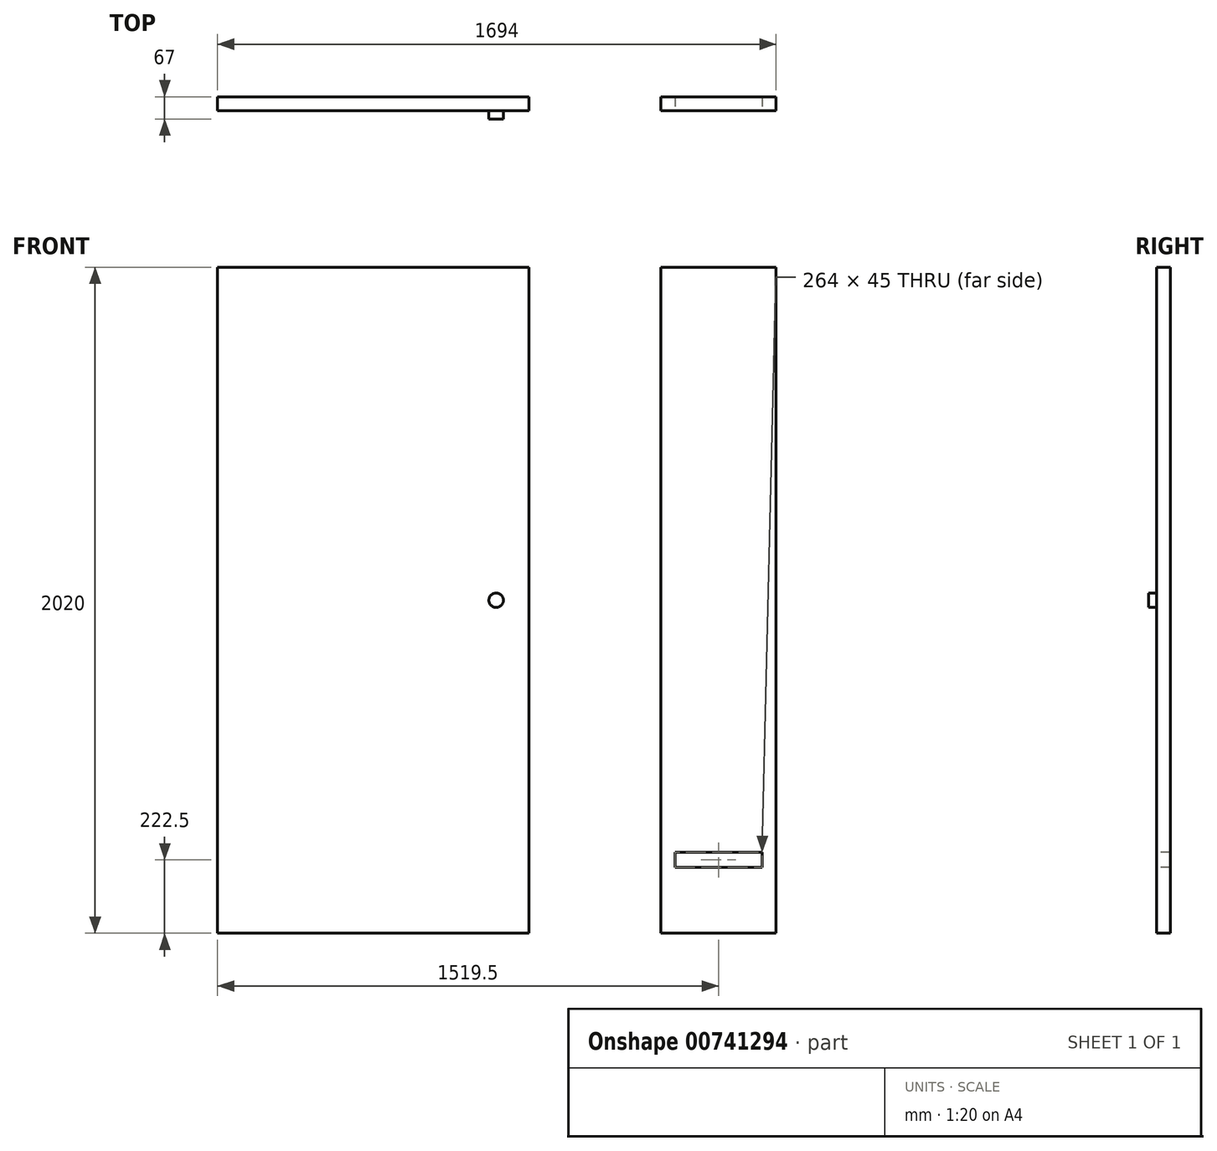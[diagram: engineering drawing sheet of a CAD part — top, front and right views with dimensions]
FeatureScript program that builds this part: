
annotation { "Feature Type Name" : "Feature", "Feature Type Description" : "" }
export const myFeature = defineFeature(function(context is Context, id is Id, definition is map)
    precondition{}
    {
        {
            var Q0;
            Q0=qCreatedBy(makeId("Front.planeOp"),FACE);
            var sketch = newSketch(context, id + "F0", { "sketchPlane" : qUnion([Q0])});
            skLineSegment(sketch, "E0.bottom", {"start": v(472.5, -1010) * mm, "end": v(-472.5, -1010) * mm});
            skLineSegment(sketch, "E0.top", {"start": v(472.5, 1010) * mm, "end": v(-472.5, 1010) * mm});
            skLineSegment(sketch, "E0.left", {"start": v(472.5, -1010) * mm, "end": v(472.5, 1010) * mm});
            skLineSegment(sketch, "E0.right", {"start": v(-472.5, -1010) * mm, "end": v(-472.5, 1010) * mm});
            skPoint(sketch, "E0.middle", {"position": v(0, 0) * mm});
            skSolve(sketch);
        }
        {
            var Q0;
            Q0 = qSketchRegion(id + "F0", true);
            extrude(context, id + "F1", {"entities" : qUnion([Q0]), "depth" : 42 * mm, "offsetDistance" : 25 * mm});
        }
        {
            var Q0;
            Q0=qCreatedBy(makeId("Front.planeOp"),FACE);
            var sketch = newSketch(context, id + "F2", { "sketchPlane" : qUnion([Q0])});
            skLineSegment(sketch, "E1.bottom", {"start": v(1221.5, -1010) * mm, "end": v(872.5, -1010) * mm});
            skLineSegment(sketch, "E1.top", {"start": v(1221.5, 1010) * mm, "end": v(872.5, 1010) * mm});
            skLineSegment(sketch, "E1.left", {"start": v(1221.5, -1010) * mm, "end": v(1221.5, 1010) * mm});
            skLineSegment(sketch, "E1.right", {"start": v(872.5, -1010) * mm, "end": v(872.5, 1010) * mm});
            skPoint(sketch, "E1.middle", {"position": v(1047, 0) * mm});
            skSolve(sketch);
        }
        {
            var Q0;
            Q0 = qSketchRegion(id + "F2", true);
            extrude(context, id + "F3", {"entities" : qUnion([Q0]), "depth" : 42 * mm, "offsetDistance" : 25 * mm});
        }
        {
            var Q0;
            Q0=makeQuery(id+"F3.opExtrude","CAP_FACE",FACE,{"disambiguationData":[OSD([sQuery(id+"F2.wireOp",EDGE,"E1.bottom"),sQuery(id+"F2.wireOp",EDGE,"E1.top"),sQuery(id+"F2.wireOp",EDGE,"E1.left"),sQuery(id+"F2.wireOp",EDGE,"E1.right")])],"isStart":false});
            var sketch = newSketch(context, id + "F4", { "sketchPlane" : qUnion([Q0])});
            skLineSegment(sketch, "E2.bottom", {"start": v(1179, -810) * mm, "end": v(915, -810) * mm});
            skLineSegment(sketch, "E2.top", {"start": v(1179, -765) * mm, "end": v(915, -765) * mm});
            skLineSegment(sketch, "E2.left", {"start": v(1179, -810) * mm, "end": v(1179, -765) * mm});
            skLineSegment(sketch, "E2.right", {"start": v(915, -810) * mm, "end": v(915, -765) * mm});
            skPoint(sketch, "E2.middle", {"position": v(1047, -787.5) * mm});
            skPoint(sketch, "E2.middle.positionSnap0", {"position": v(1047, 1010) * mm});
            skPoint(sketch, "E2.centerSnap0", {"position": v(1047, 1010) * mm});
            skSolve(sketch);
        }
        {
            var Q0;
            Q0=makeQuery(id+"F4.imprint","IMPRINT",FACE,{"disambiguationData":[TD([[makeQuery(id+"F4.imprint","IMPRINT",EDGE,{"derivedFrom":sQuery(id+"F4.wireOp",EDGE,"E2.bottom")}),-1.0]])]});
            extrude(context, id + "F5", {"entities" : qUnion([Q0]), "operationType" : NewBodyOperationType.REMOVE, "endBound" : BoundingType.THROUGH_ALL, "oppositeDirection" : true, "depth" : 25 * mm, "offsetDistance" : 25 * mm});
        }
        {
            var Q0;
            Q0=makeQuery(id+"F1.opExtrude","CAP_FACE",FACE,{"disambiguationData":[OSD([sQuery(id+"F0.wireOp",EDGE,"E0.bottom"),sQuery(id+"F0.wireOp",EDGE,"E0.top"),sQuery(id+"F0.wireOp",EDGE,"E0.left"),sQuery(id+"F0.wireOp",EDGE,"E0.right")])],"isStart":false});
            var sketch = newSketch(context, id + "F6", { "sketchPlane" : qUnion([Q0])});
            skCircle(sketch, "E3", {"center": v(372.5, 0) * mm, "radius": 22 * mm});
            skSolve(sketch);
        }
        {
            var Q0;
            Q0 = qSketchRegion(id + "F6", true);
            extrude(context, id + "F7", {"entities" : qUnion([Q0]), "operationType" : NewBodyOperationType.ADD, "depth" : 25 * mm, "offsetDistance" : 25 * mm});
        }
    });
